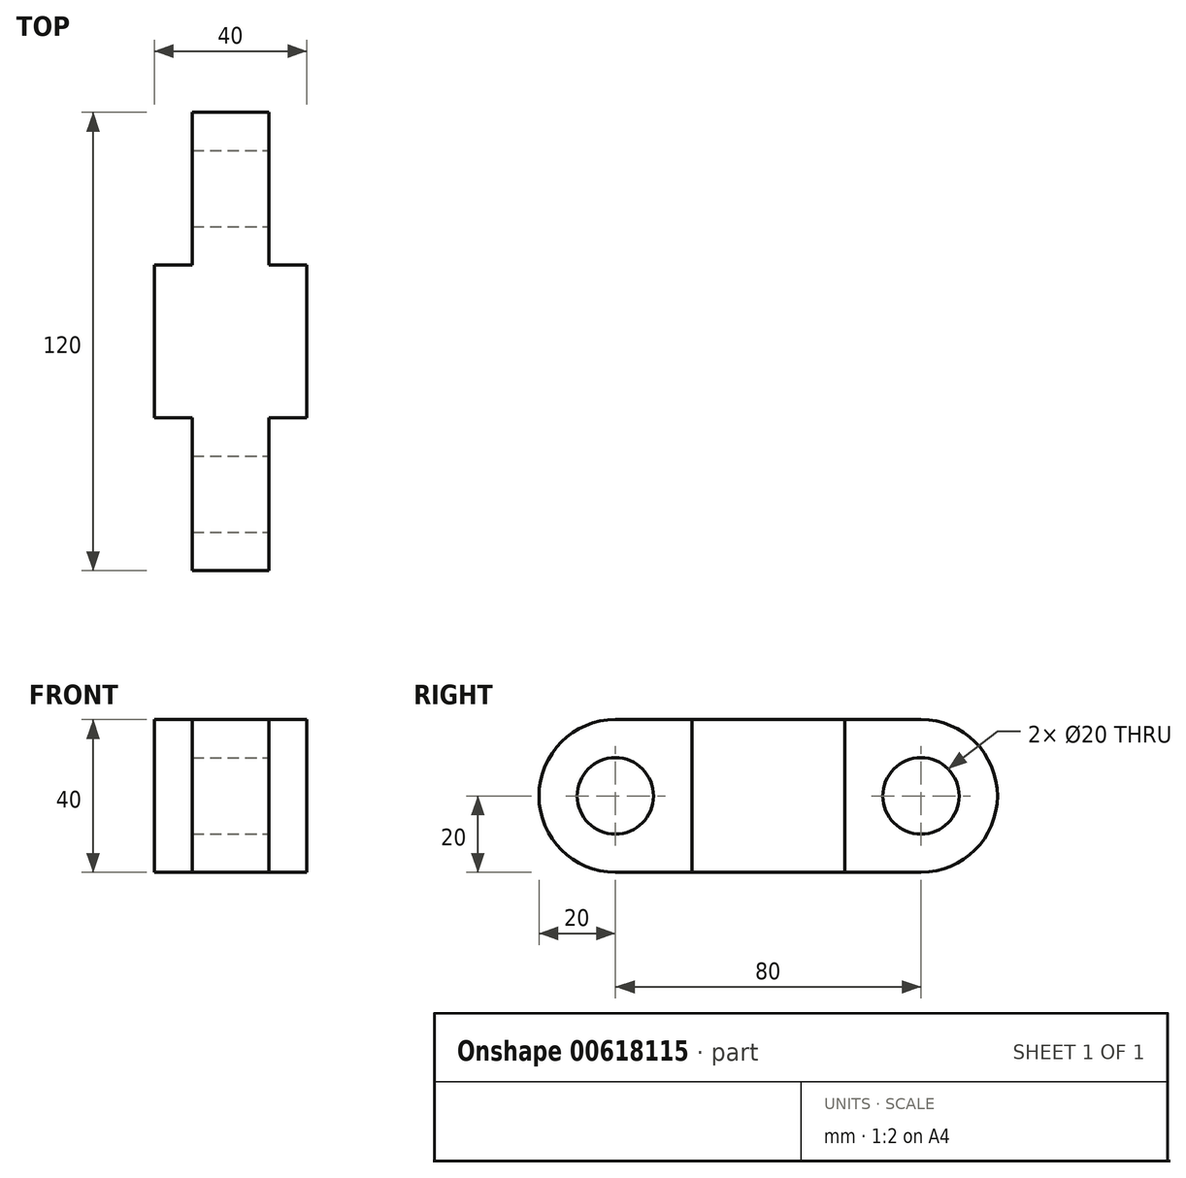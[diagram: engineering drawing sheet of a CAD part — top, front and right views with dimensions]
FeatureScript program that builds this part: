
annotation { "Feature Type Name" : "Feature", "Feature Type Description" : "" }
export const myFeature = defineFeature(function(context is Context, id is Id, definition is map)
    precondition{}
    {
        {
            var Q0;
            Q0=qCreatedBy(makeId("Top.planeOp"),FACE);
            var sketch = newSketch(context, id + "F0", { "sketchPlane" : qUnion([Q0])});
            skLineSegment(sketch, "E0.bottom", {"start": v(10, 0) * mm, "end": v(30, 0) * mm});
            skLineSegment(sketch, "E0.top", {"start": v(10, 120) * mm, "end": v(30, 120) * mm});
            skLineSegment(sketch, "E0.left", {"start": v(0, 40) * mm, "end": v(0, 80) * mm});
            skLineSegment(sketch, "E0.right", {"start": v(40, 40) * mm, "end": v(40, 80) * mm});
            skLineSegment(sketch, "E1.top", {"start": v(40, 80) * mm, "end": v(30, 80) * mm});
            skLineSegment(sketch, "E1.right", {"start": v(30, 120) * mm, "end": v(30, 80) * mm});
            skLineSegment(sketch, "E2.top", {"start": v(0, 80) * mm, "end": v(10, 80) * mm});
            skLineSegment(sketch, "E2.right", {"start": v(10, 120) * mm, "end": v(10, 80) * mm});
            skLineSegment(sketch, "E3.left", {"start": v(10, 80) * mm, "end": v(10, 80) * mm});
            skLineSegment(sketch, "E4.top", {"start": v(0, 40) * mm, "end": v(10, 40) * mm});
            skLineSegment(sketch, "E4.right", {"start": v(10, 0) * mm, "end": v(10, 40) * mm});
            skLineSegment(sketch, "E5.top", {"start": v(40, 40) * mm, "end": v(30, 40) * mm});
            skLineSegment(sketch, "E5.right", {"start": v(30, 0) * mm, "end": v(30, 40) * mm});
            skSolve(sketch);
        }
        {
            var Q0;
            Q0=makeQuery(id+"F0.imprint","IMPRINT",FACE,{"disambiguationData":[TD([[makeQuery(id+"F0.imprint","IMPRINT",EDGE,{"derivedFrom":sQuery(id+"F0.wireOp",EDGE,"E0.bottom")}),1.0]])]});
            extrude(context, id + "F1", {"entities" : qUnion([Q0]), "depth" : 40 * mm, "offsetDistance" : 25 * mm});
        }
        {
            var Q0;
            Q0=makeQuery(id+"F1.opExtrude","SWEPT_FACE",FACE,{"disambiguationData":[OSD([sQuery(id+"F0.wireOp",EDGE,"E5.right")])]});
            var sketch = newSketch(context, id + "F2", { "sketchPlane" : qUnion([Q0])});
            skPoint(sketch, "E6.centerSnap0", {"position": v(20, 0) * mm});
            skPoint(sketch, "E6.centerSnap1", {"position": v(0, 20) * mm});
            skPoint(sketch, "E6.center.orphan", {"position": v(20, 20) * mm});
            skArc(sketch, "E7", {"start": v(20, 40) * mm, "mid": v(0, 20) * mm, "end": v(20, 0) * mm});
            skLineSegment(sketch, "E8", {"start": v(20, 40) * mm, "end": v(0, 40) * mm});
            skLineSegment(sketch, "E9", {"start": v(0, 40) * mm, "end": v(0, 0) * mm});
            skLineSegment(sketch, "E10", {"start": v(0, 0) * mm, "end": v(20, 0) * mm});
            skSolve(sketch);
        }
        {
            var Q0;
            Q0 = qSketchRegion(id + "F2", true);
            extrude(context, id + "F3", {"entities" : qUnion([Q0]), "operationType" : NewBodyOperationType.REMOVE, "oppositeDirection" : true, "depth" : 20 * mm, "offsetDistance" : 25 * mm});
        }
        {
            var Q0;
            Q0=makeQuery(id+"F1.opExtrude","CAP_EDGE",EDGE,{"disambiguationData":[OSD([sQuery(id+"F0.wireOp",EDGE,"E0.top")])],"isStart":true});
            var Q1;
            Q1=makeQuery(id+"F1.opExtrude","CAP_EDGE",EDGE,{"disambiguationData":[OSD([sQuery(id+"F0.wireOp",EDGE,"E0.top")])],"isStart":false});
            fillet(context, id + "F4", {"entities" : qUnion([Q0, Q1]), "radius" : 20 * mm, "tangentPropagation" : true, "allowEdgeOverflow" : false});
        }
        {
            var Q0;
            Q0=makeQuery(id+"F1.opExtrude","SWEPT_FACE",FACE,{"disambiguationData":[OSD([sQuery(id+"F0.wireOp",EDGE,"E1.right")])]});
            var sketch = newSketch(context, id + "F5", { "sketchPlane" : qUnion([Q0])});
            skCircle(sketch, "E11", {"center": v(20, 20) * mm, "radius": 10 * mm});
            skCircle(sketch, "E12", {"center": v(100, 20) * mm, "radius": 10 * mm});
            skSolve(sketch);
        }
        {
            var Q0;
            Q0=makeQuery(id+"F5.imprint","IMPRINT",FACE,{"disambiguationData":[TD([[makeQuery(id+"F5.imprint","IMPRINT",EDGE,{"derivedFrom":sQuery(id+"F5.wireOp",EDGE,"E12")}),1.0]])]});
            var Q1;
            Q1=makeQuery(id+"F5.imprint","IMPRINT",FACE,{"disambiguationData":[TD([[makeQuery(id+"F5.imprint","IMPRINT",EDGE,{"derivedFrom":sQuery(id+"F5.wireOp",EDGE,"E11")}),1.0]])]});
            extrude(context, id + "F6", {"entities" : qUnion([Q0, Q1]), "operationType" : NewBodyOperationType.REMOVE, "oppositeDirection" : true, "depth" : 25 * mm, "offsetDistance" : 25 * mm});
        }
    });
